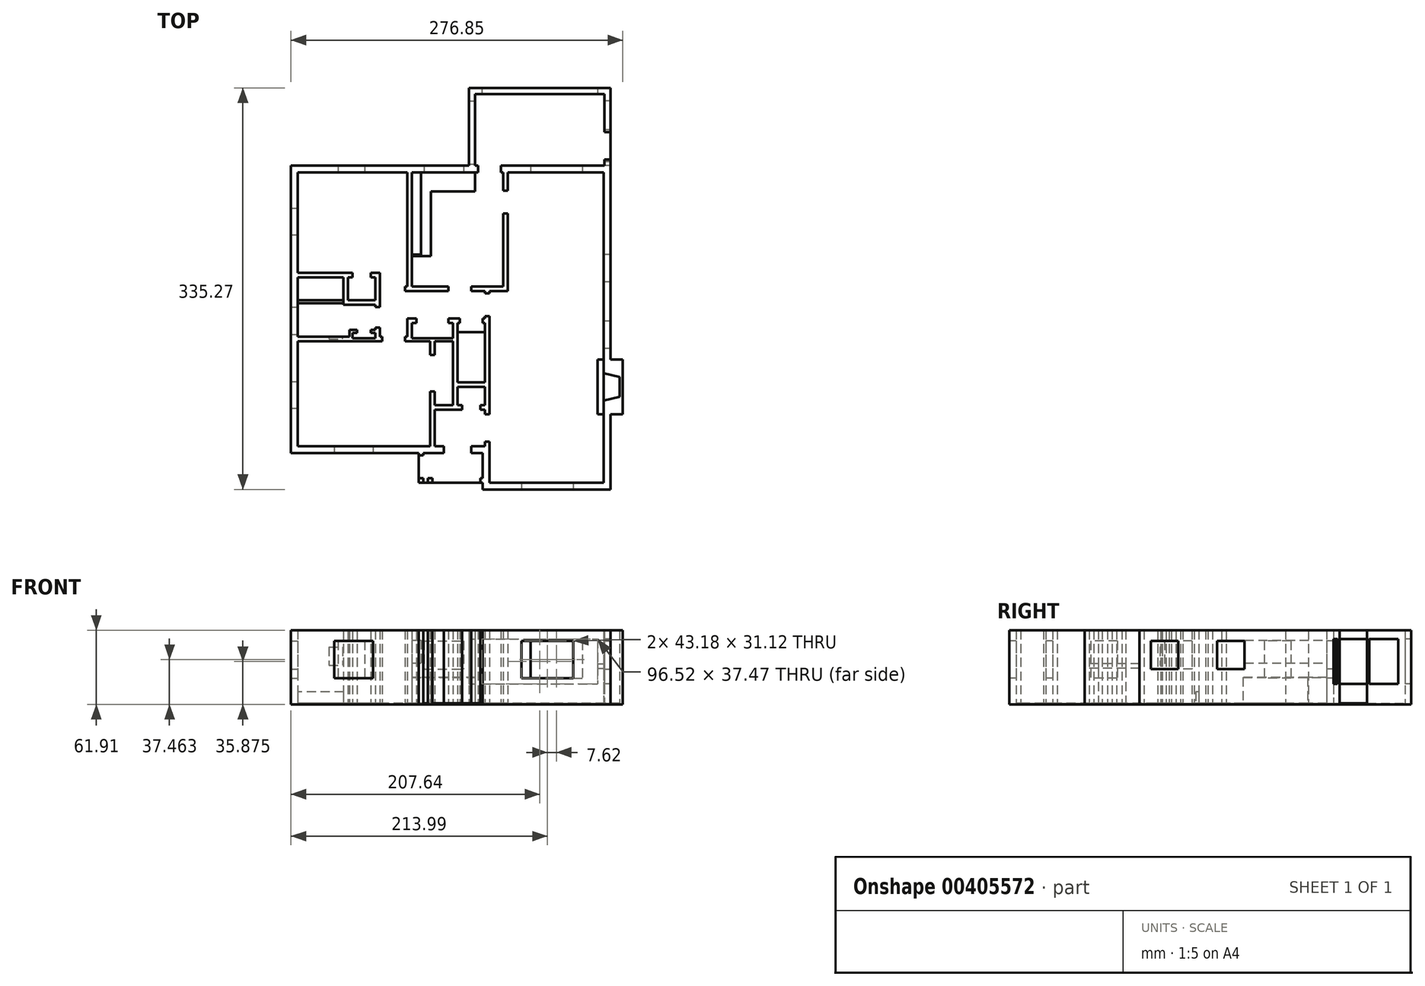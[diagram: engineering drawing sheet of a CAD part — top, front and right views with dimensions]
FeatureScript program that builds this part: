
annotation { "Feature Type Name" : "Feature", "Feature Type Description" : "" }
export const myFeature = defineFeature(function(context is Context, id is Id, definition is map)
    precondition{}
    {
        {
            var Q0;
            Q0=qCreatedBy(makeId("Top.planeOp"),FACE);
            var sketch = newSketch(context, id + "F0", { "sketchPlane" : qUnion([Q0])});
            skLineSegment(sketch, "E0.bottom", {"start": v(0, 0) * mm, "end": v(3810, 0) * mm});
            skLineSegment(sketch, "E0.top", {"start": v(-6400.8, 10363.2) * mm, "end": v(-2743.2, 10363.2) * mm});
            skLineSegment(sketch, "E0.left", {"start": v(0, 0) * mm, "end": v(0, 1219.2) * mm});
            skLineSegment(sketch, "E0.right", {"start": v(3810, 0) * mm, "end": v(3810, 10363.2) * mm});
            skLineSegment(sketch, "E1.bottom", {"start": v(-152.4, 1219.2) * mm, "end": v(-609.6, 1219.2) * mm});
            skLineSegment(sketch, "E1.right", {"start": v(-6400.8, 1219.2) * mm, "end": v(-6400.8, 4724.4) * mm});
            skLineSegment(sketch, "E2.0", {"start": v(-6629.4, 990.6) * mm, "end": v(-6629.4, 10591.8) * mm});
            skLineSegment(sketch, "E2.1", {"start": v(4038.6, -228.6) * mm, "end": v(4038.6, 10591.8) * mm});
            skLineSegment(sketch, "E2.2", {"start": v(-228.6, -228.6) * mm, "end": v(4038.6, -228.6) * mm});
            skLineSegment(sketch, "E2.3", {"start": v(-6629.4, 10591.8) * mm, "end": v(-381, 10591.8) * mm});
            skLineSegment(sketch, "E2.4", {"start": v(-228.6, -228.6) * mm, "end": v(-228.6, 990.6) * mm});
            skLineSegment(sketch, "E2.5", {"start": v(-228.6, 990.6) * mm, "end": v(-609.6, 990.6) * mm});
            skLineSegment(sketch, "E3", {"start": v(-1981.2, 1219.2) * mm, "end": v(-1981.2, 3048) * mm});
            skLineSegment(sketch, "E4", {"start": v(-1981.2, 3048) * mm, "end": v(-1828.8, 3048) * mm});
            skLineSegment(sketch, "E5", {"start": v(-1828.8, 3048) * mm, "end": v(-1828.8, 2590.8) * mm});
            skLineSegment(sketch, "E6", {"start": v(-1828.8, 2590.8) * mm, "end": v(-1219.2, 2590.8) * mm});
            skLineSegment(sketch, "E7", {"start": v(-1219.2, 2590.8) * mm, "end": v(-1219.2, 4724.4) * mm});
            skLineSegment(sketch, "E8", {"start": v(-1219.2, 4724.4) * mm, "end": v(-1828.8, 4724.4) * mm});
            skLineSegment(sketch, "E9", {"start": v(-1828.8, 4724.4) * mm, "end": v(-1828.8, 4267.2) * mm});
            skLineSegment(sketch, "E10", {"start": v(-1828.8, 4267.2) * mm, "end": v(-1981.2, 4267.2) * mm});
            skLineSegment(sketch, "E11", {"start": v(-1981.2, 4267.2) * mm, "end": v(-1981.2, 4724.4) * mm});
            skLineSegment(sketch, "E12", {"start": v(-1981.2, 4724.4) * mm, "end": v(-2819.4, 4724.4) * mm});
            skLineSegment(sketch, "E13", {"start": v(-2819.4, 4724.4) * mm, "end": v(-2819.4, 4876.8) * mm});
            skLineSegment(sketch, "E14", {"start": v(-2819.4, 4876.8) * mm, "end": v(-2743.2, 4876.8) * mm});
            skLineSegment(sketch, "E15", {"start": v(-2743.2, 4876.8) * mm, "end": v(-2743.2, 5486.4) * mm});
            skLineSegment(sketch, "E16", {"start": v(-2743.2, 5486.4) * mm, "end": v(-2438.4, 5486.4) * mm});
            skLineSegment(sketch, "E17", {"start": v(-2438.4, 5486.4) * mm, "end": v(-2438.4, 5334) * mm});
            skLineSegment(sketch, "E18", {"start": v(-2438.4, 5334) * mm, "end": v(-2590.8, 5334) * mm});
            skLineSegment(sketch, "E19", {"start": v(-2590.8, 5334) * mm, "end": v(-2590.8, 4826) * mm});
            skLineSegment(sketch, "E20", {"start": v(-2590.8, 4826) * mm, "end": v(-1219.2, 4826) * mm});
            skLineSegment(sketch, "E21", {"start": v(-1219.2, 4826) * mm, "end": v(-1219.2, 5334) * mm});
            skLineSegment(sketch, "E22", {"start": v(-1219.2, 5334) * mm, "end": v(-1371.6, 5334) * mm});
            skLineSegment(sketch, "E23", {"start": v(-1371.6, 5334) * mm, "end": v(-1371.6, 5486.4) * mm});
            skLineSegment(sketch, "E24", {"start": v(-1371.6, 5486.4) * mm, "end": v(-990.6, 5486.4) * mm});
            skLineSegment(sketch, "E25", {"start": v(-990.6, 5486.4) * mm, "end": v(-990.6, 5334) * mm});
            skLineSegment(sketch, "E26", {"start": v(-990.6, 5334) * mm, "end": v(-1066.8, 5334) * mm});
            skLineSegment(sketch, "E27", {"start": v(-1066.8, 5334) * mm, "end": v(-1066.8, 3352.8) * mm});
            skLineSegment(sketch, "E28", {"start": v(-1066.8, 2590.8) * mm, "end": v(-914.4, 2590.8) * mm});
            skLineSegment(sketch, "E29", {"start": v(-914.4, 2590.8) * mm, "end": v(-914.4, 2438.4) * mm});
            skLineSegment(sketch, "E30", {"start": v(-914.4, 2438.4) * mm, "end": v(-1828.8, 2438.4) * mm});
            skLineSegment(sketch, "E31", {"start": v(-1828.8, 2438.4) * mm, "end": v(-1828.8, 1219.2) * mm});
            skLineSegment(sketch, "E32", {"start": v(-1524, 1219.2) * mm, "end": v(-1524, 990.6) * mm});
            skLineSegment(sketch, "E33", {"start": v(-609.6, 990.6) * mm, "end": v(-609.6, 1219.2) * mm});
            skLineSegment(sketch, "E34.trimOffspring", {"start": v(-1524, 1219.2) * mm, "end": v(-1828.8, 1219.2) * mm});
            skLineSegment(sketch, "E35.trimOffspring", {"start": v(-1524, 990.6) * mm, "end": v(-6629.4, 990.6) * mm});
            skLineSegment(sketch, "E36", {"start": v(-3581.4, 4724.4) * mm, "end": v(-6400.8, 4724.4) * mm});
            skLineSegment(sketch, "E37", {"start": v(-6400.8, 4876.8) * mm, "end": v(-5359.4, 4876.8) * mm});
            skLineSegment(sketch, "E38", {"start": v(-5359.4, 4876.8) * mm, "end": v(-5359.4, 4800.6) * mm});
            skLineSegment(sketch, "E39", {"start": v(-5359.4, 4800.6) * mm, "end": v(-4902.2, 4800.6) * mm});
            skLineSegment(sketch, "E40", {"start": v(-4902.2, 4800.6) * mm, "end": v(-4902.2, 4876.8) * mm});
            skLineSegment(sketch, "E41", {"start": v(-4902.2, 4876.8) * mm, "end": v(-4673.6, 4876.8) * mm});
            skLineSegment(sketch, "E42", {"start": v(-4673.6, 4876.8) * mm, "end": v(-4673.6, 5105.4) * mm});
            skLineSegment(sketch, "E43", {"start": v(-4673.6, 5105.4) * mm, "end": v(-4419.6, 5105.4) * mm});
            skLineSegment(sketch, "E44", {"start": v(-4419.6, 5105.4) * mm, "end": v(-4419.6, 5003.8) * mm});
            skLineSegment(sketch, "E45", {"start": v(-4419.6, 5003.8) * mm, "end": v(-4572, 5003.8) * mm});
            skLineSegment(sketch, "E46", {"start": v(-4572, 5003.8) * mm, "end": v(-4572, 4826) * mm});
            skLineSegment(sketch, "E47", {"start": v(-4572, 4826) * mm, "end": v(-3810, 4826) * mm});
            skLineSegment(sketch, "E48", {"start": v(-3810, 4826) * mm, "end": v(-3810, 5003.8) * mm});
            skLineSegment(sketch, "E49", {"start": v(-3810, 5003.8) * mm, "end": v(-3962.4, 5003.8) * mm});
            skLineSegment(sketch, "E50", {"start": v(-3962.4, 5003.8) * mm, "end": v(-3962.4, 5105.4) * mm});
            skLineSegment(sketch, "E51", {"start": v(-3962.4, 5105.4) * mm, "end": v(-3810, 5105.4) * mm});
            skLineSegment(sketch, "E52", {"start": v(-3810, 5105.4) * mm, "end": v(-3810, 5181.6) * mm});
            skLineSegment(sketch, "E53", {"start": v(-3810, 5181.6) * mm, "end": v(-3657.6, 5181.6) * mm});
            skLineSegment(sketch, "E54", {"start": v(-3657.6, 5181.6) * mm, "end": v(-3657.6, 4876.8) * mm});
            skLineSegment(sketch, "E55", {"start": v(-3657.6, 4876.8) * mm, "end": v(-3581.4, 4876.8) * mm});
            skLineSegment(sketch, "E56", {"start": v(-3581.4, 4876.8) * mm, "end": v(-3581.4, 4724.4) * mm});
            skLineSegment(sketch, "E57", {"start": v(-152.4, 1219.2) * mm, "end": v(-152.4, 1371.6) * mm});
            skLineSegment(sketch, "E58", {"start": v(-152.4, 1371.6) * mm, "end": v(0, 1371.6) * mm});
            skLineSegment(sketch, "E59", {"start": v(0, 1371.6) * mm, "end": v(0, 1219.2) * mm});
            skLineSegment(sketch, "E60", {"start": v(0, 2286) * mm, "end": v(-152.4, 2286) * mm});
            skLineSegment(sketch, "E61", {"start": v(-152.4, 2286) * mm, "end": v(-152.4, 2438.4) * mm});
            skLineSegment(sketch, "E62", {"start": v(-152.4, 2438.4) * mm, "end": v(-304.8, 2438.4) * mm});
            skLineSegment(sketch, "E63", {"start": v(-304.8, 2438.4) * mm, "end": v(-304.8, 2590.8) * mm});
            skLineSegment(sketch, "E64", {"start": v(-304.8, 2590.8) * mm, "end": v(-152.4, 2590.8) * mm});
            skLineSegment(sketch, "E65", {"start": v(-152.4, 2590.8) * mm, "end": v(-152.4, 3200.4) * mm});
            skLineSegment(sketch, "E66", {"start": v(-152.4, 3200.4) * mm, "end": v(-1066.8, 3200.4) * mm});
            skLineSegment(sketch, "E67", {"start": v(-1066.8, 3352.8) * mm, "end": v(-152.4, 3352.8) * mm});
            skLineSegment(sketch, "E68", {"start": v(-152.4, 3352.8) * mm, "end": v(-152.4, 5334) * mm});
            skLineSegment(sketch, "E69", {"start": v(-152.4, 5334) * mm, "end": v(-228.6, 5334) * mm});
            skLineSegment(sketch, "E70", {"start": v(-228.6, 5334) * mm, "end": v(-228.6, 5486.4) * mm});
            skLineSegment(sketch, "E71", {"start": v(-228.6, 5486.4) * mm, "end": v(-152.4, 5486.4) * mm});
            skLineSegment(sketch, "E72", {"start": v(-152.4, 5486.4) * mm, "end": v(-152.4, 5562.6) * mm});
            skLineSegment(sketch, "E73", {"start": v(-152.4, 5562.6) * mm, "end": v(0, 5562.6) * mm});
            skLineSegment(sketch, "E74", {"start": v(0, 5562.6) * mm, "end": v(0, 2286) * mm});
            skLineSegment(sketch, "E75.trimOffspring", {"start": v(-1066.8, 3200.4) * mm, "end": v(-1066.8, 2590.8) * mm});
            skLineSegment(sketch, "E76", {"start": v(457.2, 10363.2) * mm, "end": v(457.2, 9753.6) * mm});
            skLineSegment(sketch, "E77", {"start": v(457.2, 9753.6) * mm, "end": v(609.6, 9753.6) * mm});
            skLineSegment(sketch, "E78", {"start": v(609.6, 9753.6) * mm, "end": v(609.6, 10363.2) * mm});
            skLineSegment(sketch, "E79", {"start": v(457.2, 8991.6) * mm, "end": v(457.2, 6553.2) * mm});
            skLineSegment(sketch, "E80", {"start": v(457.2, 6553.2) * mm, "end": v(-609.6, 6553.2) * mm});
            skLineSegment(sketch, "E81", {"start": v(-609.6, 6553.2) * mm, "end": v(-609.6, 6400.8) * mm});
            skLineSegment(sketch, "E82", {"start": v(-609.6, 6400.8) * mm, "end": v(-152.4, 6400.8) * mm});
            skLineSegment(sketch, "E83", {"start": v(-152.4, 6400.8) * mm, "end": v(-152.4, 6324.6) * mm});
            skLineSegment(sketch, "E84", {"start": v(-152.4, 6324.6) * mm, "end": v(0, 6324.6) * mm});
            skLineSegment(sketch, "E85", {"start": v(0, 6324.6) * mm, "end": v(0, 6400.8) * mm});
            skLineSegment(sketch, "E86", {"start": v(0, 6400.8) * mm, "end": v(609.6, 6400.8) * mm});
            skLineSegment(sketch, "E87", {"start": v(609.6, 6400.8) * mm, "end": v(609.6, 8991.6) * mm});
            skLineSegment(sketch, "E88", {"start": v(609.6, 8991.6) * mm, "end": v(457.2, 8991.6) * mm});
            skLineSegment(sketch, "E89", {"start": v(-1371.6, 6553.2) * mm, "end": v(-1371.6, 6400.8) * mm});
            skLineSegment(sketch, "E90", {"start": v(-1371.6, 6400.8) * mm, "end": v(-2819.4, 6400.8) * mm});
            skLineSegment(sketch, "E91", {"start": v(-2819.4, 6400.8) * mm, "end": v(-2819.4, 6553.2) * mm});
            skLineSegment(sketch, "E92", {"start": v(-2819.4, 6553.2) * mm, "end": v(-2743.2, 6553.2) * mm});
            skLineSegment(sketch, "E93", {"start": v(-2743.2, 6553.2) * mm, "end": v(-2743.2, 10363.2) * mm});
            skLineSegment(sketch, "E94", {"start": v(-2590.8, 10363.2) * mm, "end": v(-2590.8, 6553.2) * mm});
            skLineSegment(sketch, "E95", {"start": v(-2590.8, 6553.2) * mm, "end": v(-1371.6, 6553.2) * mm});
            skLineSegment(sketch, "E96", {"start": v(-6400.8, 7010.4) * mm, "end": v(-4572, 7010.4) * mm});
            skLineSegment(sketch, "E97", {"start": v(-4572, 7010.4) * mm, "end": v(-4572, 6858) * mm});
            skLineSegment(sketch, "E98", {"start": v(-4572, 6858) * mm, "end": v(-4724.4, 6858) * mm});
            skLineSegment(sketch, "E99", {"start": v(-4724.4, 6858) * mm, "end": v(-4724.4, 6096) * mm});
            skLineSegment(sketch, "E100", {"start": v(-4724.4, 6096) * mm, "end": v(-3810, 6096) * mm});
            skLineSegment(sketch, "E101", {"start": v(-3810, 6096) * mm, "end": v(-3810, 6858) * mm});
            skLineSegment(sketch, "E102", {"start": v(-3810, 6858) * mm, "end": v(-3962.4, 6858) * mm});
            skLineSegment(sketch, "E103", {"start": v(-3962.4, 6858) * mm, "end": v(-3962.4, 7010.4) * mm});
            skLineSegment(sketch, "E104", {"start": v(-3962.4, 7010.4) * mm, "end": v(-3657.6, 7010.4) * mm});
            skLineSegment(sketch, "E105", {"start": v(-3657.6, 7010.4) * mm, "end": v(-3657.6, 5867.4) * mm});
            skLineSegment(sketch, "E106", {"start": v(-3657.6, 5867.4) * mm, "end": v(-3810, 5867.4) * mm});
            skLineSegment(sketch, "E107", {"start": v(-3810, 5867.4) * mm, "end": v(-3810, 5943.6) * mm});
            skLineSegment(sketch, "E108", {"start": v(-3810, 5943.6) * mm, "end": v(-4876.8, 5943.6) * mm});
            skLineSegment(sketch, "E109", {"start": v(-4876.8, 5943.6) * mm, "end": v(-4876.8, 6858) * mm});
            skLineSegment(sketch, "E110", {"start": v(-4876.8, 6858) * mm, "end": v(-6400.8, 6858) * mm});
            skText(sketch, "E111", { "text": "All doors are 80in tall", "fontName": "OpenSans-Regular.ttf"});
            skLineSegment(sketch, "E112", {"start": v(381, 10363.2) * mm, "end": v(381, 10591.8) * mm});
            skLineSegment(sketch, "E113", {"start": v(-381, 10363.2) * mm, "end": v(-381, 10591.8) * mm});
            skLineSegment(sketch, "E114.trimOffspring", {"start": v(381, 10591.8) * mm, "end": v(4038.6, 10591.8) * mm});
            skLineSegment(sketch, "E115.trimOffspring", {"start": v(381, 10363.2) * mm, "end": v(457.2, 10363.2) * mm});
            skLineSegment(sketch, "E116", {"start": v(-5359.4, 4876.8) * mm, "end": v(-4902.2, 4876.8) * mm});
            skLineSegment(sketch, "E117", {"start": v(-4876.8, 5994.4) * mm, "end": v(-6400.8, 5994.4) * mm});
            skLineSegment(sketch, "E118", {"start": v(-6400.8, 6070.6) * mm, "end": v(-4876.8, 6070.6) * mm});
            skLineSegment(sketch, "E119", {"start": v(4038.6, 2286) * mm, "end": v(4445, 2286) * mm});
            skLineSegment(sketch, "E120", {"start": v(4445, 2286) * mm, "end": v(4445, 4114.8) * mm});
            skLineSegment(sketch, "E121", {"start": v(4445, 4114.8) * mm, "end": v(4038.6, 4114.8) * mm});
            skLineSegment(sketch, "E122", {"start": v(3810, 3657.6) * mm, "end": v(4343.4, 3530.6) * mm});
            skLineSegment(sketch, "E123", {"start": v(4343.4, 3530.6) * mm, "end": v(4343.4, 2870.2) * mm});
            skLineSegment(sketch, "E124", {"start": v(4343.4, 2870.2) * mm, "end": v(3810, 2743.2) * mm});
            skLineSegment(sketch, "E125", {"start": v(4343.4, 3200.4) * mm, "end": v(4445, 3200.4) * mm, "construction": true});
            skLineSegment(sketch, "E126.trimOffspring", {"start": v(-1981.2, 1219.2) * mm, "end": v(-6400.8, 1219.2) * mm});
            skLineSegment(sketch, "E127.trimOffspring", {"start": v(-2590.8, 10363.2) * mm, "end": v(-381, 10363.2) * mm});
            skLineSegment(sketch, "E128.trimOffspring", {"start": v(609.6, 10363.2) * mm, "end": v(3810, 10363.2) * mm});
            skLineSegment(sketch, "E129.trimOffspring", {"start": v(-6400.8, 4876.8) * mm, "end": v(-6400.8, 6858) * mm});
            skLineSegment(sketch, "E130.trimOffspring", {"start": v(-6400.8, 7010.4) * mm, "end": v(-6400.8, 10363.2) * mm});
            skLineSegment(sketch, "E131", {"start": v(4038.6, 10591.8) * mm, "end": v(4038.6, 13182.6) * mm});
            skLineSegment(sketch, "E132", {"start": v(4038.6, 13182.6) * mm, "end": v(-685.8, 13182.6) * mm});
            skLineSegment(sketch, "E133", {"start": v(-685.8, 13182.6) * mm, "end": v(-685.8, 10591.8) * mm});
            skLineSegment(sketch, "E134", {"start": v(3835.4, 10591.8) * mm, "end": v(3835.4, 12979.4) * mm});
            skLineSegment(sketch, "E135", {"start": v(3835.4, 12979.4) * mm, "end": v(-482.6, 12979.4) * mm});
            skLineSegment(sketch, "E136", {"start": v(-482.6, 12979.4) * mm, "end": v(-482.6, 10591.8) * mm});
            skLineSegment(sketch, "E137", {"start": v(-2362.2, 990.6) * mm, "end": v(-2362.2, 0) * mm});
            skLineSegment(sketch, "E138", {"start": v(-2362.2, 0) * mm, "end": v(-228.6, 0) * mm});
            skLineSegment(sketch, "E139", {"start": v(-2362.2, 152.4) * mm, "end": v(-2209.8, 152.4) * mm});
            skLineSegment(sketch, "E140", {"start": v(-2209.8, 152.4) * mm, "end": v(-2209.8, 0) * mm});
            skLineSegment(sketch, "E141", {"start": v(-2057.4, 0) * mm, "end": v(-2057.4, 152.4) * mm});
            skLineSegment(sketch, "E142", {"start": v(-2057.4, 152.4) * mm, "end": v(-1905, 152.4) * mm});
            skLineSegment(sketch, "E143", {"start": v(-1905, 152.4) * mm, "end": v(-1905, 0) * mm});
            skLineSegment(sketch, "E144", {"start": v(-304.8, 0) * mm, "end": v(-304.8, 152.4) * mm});
            skLineSegment(sketch, "E145", {"start": v(-304.8, 152.4) * mm, "end": v(-228.6, 152.4) * mm});
            skLineSegment(sketch, "E146", {"start": v(-2209.8, 990.6) * mm, "end": v(-2209.8, 914.4) * mm});
            skLineSegment(sketch, "E147", {"start": v(-2209.8, 914.4) * mm, "end": v(-2362.2, 914.4) * mm});
            skLineSegment(sketch, "E148", {"start": v(3835.4, 10795) * mm, "end": v(4038.6, 10795) * mm});
            skLineSegment(sketch, "E149", {"start": v(3835.4, 11709.4) * mm, "end": v(4038.6, 11709.4) * mm});
            const initialGuessF0  = {"E111": [1.17516, -1.09779, 1, 0, 0.12028]};
            skSetInitialGuess(sketch, initialGuessF0);
            skSolve(sketch);
        }
        {
            var Q0;
            {var subQ3=sQuery(id+"F0.wireOp",EDGE,"E132");Q0=makeQuery(id+"F0.imprint","IMPRINT",FACE,{"disambiguationData":[TD([[makeQuery(id+"F0.imprint","IMPRINT",EDGE,{"derivedFrom":subQ3}),1.0]])]});}
            var Q1;
            {var subQ5=sQuery(id+"F0.wireOp",EDGE,"E148");Q1=makeQuery(id+"F0.imprint","IMPRINT",FACE,{"disambiguationData":[TD([[makeQuery(id+"F0.imprint","IMPRINT",EDGE,{"derivedFrom":subQ5}),-1.0]])]});}
            var Q2;
            Q2=makeQuery(id+"F0.imprint","IMPRINT",FACE,{"disambiguationData":[TD([[makeQuery(id+"F0.imprint","IMPRINT",EDGE,{"derivedFrom":sQuery(id+"F0.wireOp",EDGE,"E76")}),1.0]])]});
            var Q3;
            Q3=makeQuery(id+"F0.imprint","IMPRINT",FACE,{"disambiguationData":[TD([[makeQuery(id+"F0.imprint","IMPRINT",EDGE,{"derivedFrom":sQuery(id+"F0.wireOp",EDGE,"E0.top")}),1.0]])]});
            var Q4;
            Q4=makeQuery(id+"F0.imprint","IMPRINT",FACE,{"disambiguationData":[TD([[makeQuery(id+"F0.imprint","IMPRINT",EDGE,{"derivedFrom":sQuery(id+"F0.wireOp",EDGE,"E79")}),1.0]])]});
            var Q5;
            {var subQ0=sQuery(id+"F0.wireOp",EDGE,"E119");Q5=makeQuery(id+"F0.imprint","IMPRINT",FACE,{"disambiguationData":[TD([[makeQuery(id+"F0.imprint","IMPRINT",EDGE,{"derivedFrom":subQ0}),1.0]])]});}
            var Q6;
            {var subQ11=sQuery(id+"F0.wireOp",EDGE,"E0.bottom");Q6=makeQuery(id+"F0.imprint","IMPRINT",FACE,{"disambiguationData":[TD([[makeQuery(id+"F0.imprint","IMPRINT",EDGE,{"derivedFrom":subQ11}),-1.0]])]});}
            var Q7;
            Q7=makeQuery(id+"F0.imprint","IMPRINT",FACE,{"disambiguationData":[TD([[makeQuery(id+"F0.imprint","IMPRINT",EDGE,{"derivedFrom":sQuery(id+"F0.wireOp",EDGE,"E38")}),1.0]])]});
            var Q8;
            {var subQ3=sQuery(id+"F0.wireOp",EDGE,"E139");Q8=makeQuery(id+"F0.imprint","IMPRINT",FACE,{"disambiguationData":[TD([[makeQuery(id+"F0.imprint","IMPRINT",EDGE,{"derivedFrom":subQ3}),-1.0]])]});}
            var Q9;
            {var subQ0=sQuery(id+"F0.wireOp",EDGE,"E141");Q9=makeQuery(id+"F0.imprint","IMPRINT",FACE,{"disambiguationData":[TD([[makeQuery(id+"F0.imprint","IMPRINT",EDGE,{"derivedFrom":subQ0}),-1.0]])]});}
            var Q10;
            {var subQ3=sQuery(id+"F0.wireOp",EDGE,"E146");Q10=makeQuery(id+"F0.imprint","IMPRINT",FACE,{"disambiguationData":[TD([[makeQuery(id+"F0.imprint","IMPRINT",EDGE,{"derivedFrom":subQ3}),-1.0]])]});}
            var Q11;
            {var subQ4=sQuery(id+"F0.wireOp",EDGE,"E144");Q11=makeQuery(id+"F0.imprint","IMPRINT",FACE,{"disambiguationData":[TD([[makeQuery(id+"F0.imprint","IMPRINT",EDGE,{"derivedFrom":subQ4}),-1.0]])]});}
            extrude(context, id + "F1", {"entities" : qUnion([Q0, Q1, Q2, Q3, Q4, Q5, Q6, Q7, Q8, Q9, Q10, Q11]), "depth" : 2438.4 * mm, "offsetDistance" : 25.4 * mm});
        }
        {
            var Q0;
            {var subQ5=sQuery(id+"F0.wireOp",EDGE,"E123");Q0=makeQuery(id+"F0.imprint","IMPRINT",FACE,{"disambiguationData":[TD([[makeQuery(id+"F0.imprint","IMPRINT",EDGE,{"derivedFrom":subQ5}),-1.0]])]});}
            var Q1;
            {var subQ0=sQuery(id+"F0.wireOp",EDGE,"E122");var subQ1=sQuery(id+"F0.wireOp",EDGE,"E0.right");var subQ2=makeQuery(id+"F0.imprint","INTERSECT",VERTEX,{"derivedFrom":[subQ1,subQ0]});Q1=makeQuery(id+"F0.imprint","IMPRINT",FACE,{"disambiguationData":[TD([[makeQuery(id+"F0.imprint","IMPRINT",EDGE,{"disambiguationData":[TD([[subQ2,1.0]])],"derivedFrom":subQ1}),-1.0]])]});}
            var Q2;
            Q2=makeQuery(id+"F0.imprint","IMPRINT",FACE,{"disambiguationData":[TD([[makeQuery(id+"F0.imprint","IMPRINT",EDGE,{"derivedFrom":sQuery(id+"F0.wireOp",EDGE,"E79")}),1.0]])]});
            var Q3;
            {var subQ0=sQuery(id+"F0.wireOp",EDGE,"E110");Q3=makeQuery(id+"F0.imprint","IMPRINT",FACE,{"disambiguationData":[TD([[makeQuery(id+"F0.imprint","IMPRINT",EDGE,{"derivedFrom":subQ0}),1.0]])]});}
            var Q4;
            {var subQ0=sQuery(id+"F0.wireOp",EDGE,"E117");Q4=makeQuery(id+"F0.imprint","IMPRINT",FACE,{"disambiguationData":[TD([[makeQuery(id+"F0.imprint","IMPRINT",EDGE,{"derivedFrom":subQ0}),-1.0]])]});}
            var Q5;
            Q5=makeQuery(id+"F0.imprint","IMPRINT",FACE,{"disambiguationData":[TD([[makeQuery(id+"F0.imprint","IMPRINT",EDGE,{"derivedFrom":sQuery(id+"F0.wireOp",EDGE,"E38")}),1.0]])]});
            var Q6;
            {var subQ19=sQuery(id+"F0.wireOp",EDGE,"E0.bottom");Q6=makeQuery(id+"F0.imprint","IMPRINT",FACE,{"disambiguationData":[TD([[makeQuery(id+"F0.imprint","IMPRINT",EDGE,{"derivedFrom":subQ19}),1.0]])]});}
            var Q7;
            Q7=makeQuery(id+"F0.imprint","IMPRINT",FACE,{"disambiguationData":[TD([[makeQuery(id+"F0.imprint","IMPRINT",EDGE,{"derivedFrom":sQuery(id+"F0.wireOp",EDGE,"E0.top")}),1.0]])]});
            var Q8;
            {var subQ3=sQuery(id+"F0.wireOp",EDGE,"E146");Q8=makeQuery(id+"F0.imprint","IMPRINT",FACE,{"disambiguationData":[TD([[makeQuery(id+"F0.imprint","IMPRINT",EDGE,{"derivedFrom":subQ3}),-1.0]])]});}
            var Q9;
            {var subQ3=sQuery(id+"F0.wireOp",EDGE,"E139");Q9=makeQuery(id+"F0.imprint","IMPRINT",FACE,{"disambiguationData":[TD([[makeQuery(id+"F0.imprint","IMPRINT",EDGE,{"derivedFrom":subQ3}),-1.0]])]});}
            var Q10;
            {var subQ0=sQuery(id+"F0.wireOp",EDGE,"E141");Q10=makeQuery(id+"F0.imprint","IMPRINT",FACE,{"disambiguationData":[TD([[makeQuery(id+"F0.imprint","IMPRINT",EDGE,{"derivedFrom":subQ0}),-1.0]])]});}
            var Q11;
            {var subQ3=sQuery(id+"F0.wireOp",EDGE,"E132");Q11=makeQuery(id+"F0.imprint","IMPRINT",FACE,{"disambiguationData":[TD([[makeQuery(id+"F0.imprint","IMPRINT",EDGE,{"derivedFrom":subQ3}),1.0]])]});}
            var Q12;
            {var subQ0=sQuery(id+"F0.wireOp",EDGE,"E148");Q12=makeQuery(id+"F0.imprint","IMPRINT",FACE,{"disambiguationData":[TD([[makeQuery(id+"F0.imprint","IMPRINT",EDGE,{"derivedFrom":subQ0}),1.0]])]});}
            var Q13;
            Q13=makeQuery(id+"F0.imprint","IMPRINT",FACE,{"disambiguationData":[TD([[makeQuery(id+"F0.imprint","IMPRINT",EDGE,{"derivedFrom":sQuery(id+"F0.wireOp",EDGE,"E76")}),1.0]])]});
            var Q14;
            {var subQ5=sQuery(id+"F0.wireOp",EDGE,"E148");Q14=makeQuery(id+"F0.imprint","IMPRINT",FACE,{"disambiguationData":[TD([[makeQuery(id+"F0.imprint","IMPRINT",EDGE,{"derivedFrom":subQ5}),-1.0]])]});}
            var Q15;
            {var subQ0=sQuery(id+"F0.wireOp",EDGE,"E119");Q15=makeQuery(id+"F0.imprint","IMPRINT",FACE,{"disambiguationData":[TD([[makeQuery(id+"F0.imprint","IMPRINT",EDGE,{"derivedFrom":subQ0}),1.0]])]});}
            var Q16;
            {var subQ11=sQuery(id+"F0.wireOp",EDGE,"E0.bottom");Q16=makeQuery(id+"F0.imprint","IMPRINT",FACE,{"disambiguationData":[TD([[makeQuery(id+"F0.imprint","IMPRINT",EDGE,{"derivedFrom":subQ11}),-1.0]])]});}
            var Q17;
            {var subQ4=sQuery(id+"F0.wireOp",EDGE,"E144");Q17=makeQuery(id+"F0.imprint","IMPRINT",FACE,{"disambiguationData":[TD([[makeQuery(id+"F0.imprint","IMPRINT",EDGE,{"derivedFrom":subQ4}),-1.0]])]});}
            extrude(context, id + "F2", {"entities" : qUnion([Q0, Q1, Q2, Q3, Q4, Q5, Q6, Q7, Q8, Q9, Q10, Q11, Q12, Q13, Q14, Q15, Q16, Q17]), "operationType" : NewBodyOperationType.ADD, "oppositeDirection" : true, "depth" : 38.1 * mm, "offsetDistance" : 25.4 * mm});
        }
        {
            var Q0;
            Q0=qCreatedBy(makeId("Top.planeOp"),FACE);
            var sketch = newSketch(context, id + "F3", { "sketchPlane" : qUnion([Q0])});
            skLineSegment(sketch, "E150", {"start": v(-482.6, 10363.2) * mm, "end": v(-482.6, 9728.2) * mm});
            skLineSegment(sketch, "E151", {"start": v(-482.6, 9728.2) * mm, "end": v(-1955.8, 9728.2) * mm});
            skLineSegment(sketch, "E152", {"start": v(-1955.8, 9728.2) * mm, "end": v(-1955.8, 7569.2) * mm});
            skLineSegment(sketch, "E153", {"start": v(-1955.8, 7569.2) * mm, "end": v(-2590.8, 7569.2) * mm});
            skLineSegment(sketch, "E154", {"start": v(-2590.8, 7569.2) * mm, "end": v(-2590.8, 10363.2) * mm});
            skLineSegment(sketch, "E155", {"start": v(-2590.8, 10363.2) * mm, "end": v(-482.6, 10363.2) * mm});
            skLineSegment(sketch, "E156", {"start": v(-1955.8, 7569.2) * mm, "end": v(-1879.6, 7569.2) * mm});
            skLineSegment(sketch, "E157", {"start": v(-1879.6, 7569.2) * mm, "end": v(-1879.6, 6807.2) * mm});
            skLineSegment(sketch, "E158", {"start": v(-1879.6, 6807.2) * mm, "end": v(-2590.8, 6807.2) * mm});
            skLineSegment(sketch, "E159", {"start": v(-2590.8, 6807.2) * mm, "end": v(-2590.8, 7569.2) * mm});
            skLineSegment(sketch, "E160.bottom", {"start": v(457.2, 6908.8) * mm, "end": v(-457.2, 6908.8) * mm});
            skLineSegment(sketch, "E160.top", {"start": v(457.2, 7823.2) * mm, "end": v(-457.2, 7823.2) * mm});
            skLineSegment(sketch, "E160.left", {"start": v(457.2, 6908.8) * mm, "end": v(457.2, 7823.2) * mm});
            skLineSegment(sketch, "E160.right", {"start": v(-457.2, 6908.8) * mm, "end": v(-457.2, 7823.2) * mm});
            skLineSegment(sketch, "E161.bottom", {"start": v(0, 7823.2) * mm, "end": v(457.2, 7823.2) * mm});
            skLineSegment(sketch, "E161.top", {"start": v(0, 8737.6) * mm, "end": v(457.2, 8737.6) * mm});
            skLineSegment(sketch, "E161.left", {"start": v(0, 7823.2) * mm, "end": v(0, 8737.6) * mm});
            skLineSegment(sketch, "E161.right", {"start": v(457.2, 7823.2) * mm, "end": v(457.2, 8737.6) * mm});
            skLineSegment(sketch, "E162.bottom", {"start": v(-2590.8, 10363.2) * mm, "end": v(-2286, 10363.2) * mm});
            skLineSegment(sketch, "E162.top", {"start": v(-2590.8, 7620) * mm, "end": v(-2286, 7620) * mm});
            skLineSegment(sketch, "E162.left", {"start": v(-2590.8, 10363.2) * mm, "end": v(-2590.8, 7620) * mm});
            skLineSegment(sketch, "E162.right", {"start": v(-2286, 10363.2) * mm, "end": v(-2286, 7620) * mm});
            skLineSegment(sketch, "E163.bottom", {"start": v(-5054.6, 10591.8) * mm, "end": v(-4165.6, 10591.8) * mm});
            skLineSegment(sketch, "E163.top", {"start": v(-5054.6, 10363.2) * mm, "end": v(-4165.6, 10363.2) * mm});
            skLineSegment(sketch, "E163.left", {"start": v(-5054.6, 10591.8) * mm, "end": v(-5054.6, 10363.2) * mm});
            skLineSegment(sketch, "E163.right", {"start": v(-4165.6, 10591.8) * mm, "end": v(-4165.6, 10363.2) * mm});
            skLineSegment(sketch, "E164.bottom", {"start": v(-6629.4, 9169.4) * mm, "end": v(-6400.8, 9169.4) * mm});
            skLineSegment(sketch, "E164.top", {"start": v(-6629.4, 8280.4) * mm, "end": v(-6400.8, 8280.4) * mm});
            skLineSegment(sketch, "E164.left", {"start": v(-6629.4, 9169.4) * mm, "end": v(-6629.4, 8280.4) * mm});
            skLineSegment(sketch, "E164.right", {"start": v(-6400.8, 9169.4) * mm, "end": v(-6400.8, 8280.4) * mm});
            skLineSegment(sketch, "E165.bottom", {"start": v(-6629.4, 5867.4) * mm, "end": v(-6400.8, 5867.4) * mm});
            skLineSegment(sketch, "E165.top", {"start": v(-6629.4, 4953) * mm, "end": v(-6400.8, 4953) * mm});
            skLineSegment(sketch, "E165.left", {"start": v(-6629.4, 5867.4) * mm, "end": v(-6629.4, 4953) * mm});
            skLineSegment(sketch, "E165.right", {"start": v(-6400.8, 5867.4) * mm, "end": v(-6400.8, 4953) * mm});
            skLineSegment(sketch, "E166.bottom", {"start": v(-6629.4, 3378.2) * mm, "end": v(-6400.8, 3378.2) * mm});
            skLineSegment(sketch, "E166.top", {"start": v(-6629.4, 2489.2) * mm, "end": v(-6400.8, 2489.2) * mm});
            skLineSegment(sketch, "E166.left", {"start": v(-6629.4, 3378.2) * mm, "end": v(-6629.4, 2489.2) * mm});
            skLineSegment(sketch, "E166.right", {"start": v(-6400.8, 3378.2) * mm, "end": v(-6400.8, 2489.2) * mm});
            skLineSegment(sketch, "E167.bottom", {"start": v(-5181.6, 1219.2) * mm, "end": v(-3886.2, 1219.2) * mm});
            skLineSegment(sketch, "E167.top", {"start": v(-5181.6, 990.6) * mm, "end": v(-3886.2, 990.6) * mm});
            skLineSegment(sketch, "E167.left", {"start": v(-5181.6, 1219.2) * mm, "end": v(-5181.6, 990.6) * mm});
            skLineSegment(sketch, "E167.right", {"start": v(-3886.2, 1219.2) * mm, "end": v(-3886.2, 990.6) * mm});
            skLineSegment(sketch, "E168.bottom", {"start": v(1066.8, 0) * mm, "end": v(2794, 0) * mm});
            skLineSegment(sketch, "E168.top", {"start": v(1066.8, -228.6) * mm, "end": v(2794, -228.6) * mm});
            skLineSegment(sketch, "E168.left", {"start": v(1066.8, 0) * mm, "end": v(1066.8, -228.6) * mm});
            skLineSegment(sketch, "E168.right", {"start": v(2794, 0) * mm, "end": v(2794, -228.6) * mm});
            skLineSegment(sketch, "E169.bottom", {"start": v(3810, 5410.2) * mm, "end": v(4038.6, 5410.2) * mm});
            skLineSegment(sketch, "E169.top", {"start": v(3810, 4495.8) * mm, "end": v(4038.6, 4495.8) * mm});
            skLineSegment(sketch, "E169.left", {"start": v(3810, 5410.2) * mm, "end": v(3810, 4495.8) * mm});
            skLineSegment(sketch, "E169.right", {"start": v(4038.6, 5410.2) * mm, "end": v(4038.6, 4495.8) * mm});
            skLineSegment(sketch, "E170.bottom", {"start": v(4038.6, 6705.6) * mm, "end": v(3810, 6705.6) * mm});
            skLineSegment(sketch, "E170.top", {"start": v(4038.6, 7620) * mm, "end": v(3810, 7620) * mm});
            skLineSegment(sketch, "E170.left", {"start": v(4038.6, 6705.6) * mm, "end": v(4038.6, 7620) * mm});
            skLineSegment(sketch, "E170.right", {"start": v(3810, 6705.6) * mm, "end": v(3810, 7620) * mm});
            skLineSegment(sketch, "E171.bottom", {"start": v(1371.6, 10591.8) * mm, "end": v(3098.8, 10591.8) * mm});
            skLineSegment(sketch, "E171.top", {"start": v(1371.6, 10363.2) * mm, "end": v(3098.8, 10363.2) * mm});
            skLineSegment(sketch, "E171.left", {"start": v(1371.6, 10591.8) * mm, "end": v(1371.6, 10363.2) * mm});
            skLineSegment(sketch, "E171.right", {"start": v(3098.8, 10591.8) * mm, "end": v(3098.8, 10363.2) * mm});
            skLineSegment(sketch, "E172.bottom", {"start": v(-2184.4, 10591.8) * mm, "end": v(-863.6, 10591.8) * mm});
            skLineSegment(sketch, "E172.top", {"start": v(-2184.4, 10363.2) * mm, "end": v(-863.6, 10363.2) * mm});
            skLineSegment(sketch, "E172.left", {"start": v(-2184.4, 10591.8) * mm, "end": v(-2184.4, 10363.2) * mm});
            skLineSegment(sketch, "E172.right", {"start": v(-863.6, 10591.8) * mm, "end": v(-863.6, 10363.2) * mm});
            skLineSegment(sketch, "E173.bottom", {"start": v(-685.8, 12750.8) * mm, "end": v(-482.6, 12750.8) * mm});
            skLineSegment(sketch, "E173.top", {"start": v(-685.8, 10642.6) * mm, "end": v(-482.6, 10642.6) * mm});
            skLineSegment(sketch, "E173.left", {"start": v(-685.8, 12750.8) * mm, "end": v(-685.8, 10642.6) * mm});
            skLineSegment(sketch, "E173.right", {"start": v(-482.6, 12750.8) * mm, "end": v(-482.6, 10642.6) * mm});
            skLineSegment(sketch, "E174.bottom", {"start": v(-254, 13182.6) * mm, "end": v(3606.8, 13182.6) * mm});
            skLineSegment(sketch, "E174.top", {"start": v(-254, 12979.4) * mm, "end": v(3606.8, 12979.4) * mm});
            skLineSegment(sketch, "E174.left", {"start": v(-254, 13182.6) * mm, "end": v(-254, 12979.4) * mm});
            skLineSegment(sketch, "E174.right", {"start": v(3606.8, 13182.6) * mm, "end": v(3606.8, 12979.4) * mm});
            skLineSegment(sketch, "E175.bottom", {"start": v(4038.6, 12750.8) * mm, "end": v(3835.4, 12750.8) * mm});
            skLineSegment(sketch, "E175.top", {"start": v(4038.6, 11785.6) * mm, "end": v(3835.4, 11785.6) * mm});
            skLineSegment(sketch, "E175.left", {"start": v(4038.6, 12750.8) * mm, "end": v(4038.6, 11785.6) * mm});
            skLineSegment(sketch, "E175.right", {"start": v(3835.4, 12750.8) * mm, "end": v(3835.4, 11785.6) * mm});
            skLineSegment(sketch, "E176.bottom", {"start": v(4038.6, 10591.8) * mm, "end": v(3835.4, 10591.8) * mm});
            skLineSegment(sketch, "E176.top", {"start": v(4038.6, 10718.8) * mm, "end": v(3835.4, 10718.8) * mm});
            skLineSegment(sketch, "E176.left", {"start": v(4038.6, 10591.8) * mm, "end": v(4038.6, 10718.8) * mm});
            skLineSegment(sketch, "E176.right", {"start": v(3835.4, 10591.8) * mm, "end": v(3835.4, 10718.8) * mm});
            skLineSegment(sketch, "E177.bottom", {"start": v(3606.8, 4114.8) * mm, "end": v(3810, 4114.8) * mm});
            skLineSegment(sketch, "E177.top", {"start": v(3606.8, 2286) * mm, "end": v(3810, 2286) * mm});
            skLineSegment(sketch, "E177.left", {"start": v(3606.8, 4114.8) * mm, "end": v(3606.8, 2286) * mm});
            skLineSegment(sketch, "E177.right", {"start": v(3810, 4114.8) * mm, "end": v(3810, 2286) * mm});
            skLineSegment(sketch, "E178.bottom", {"start": v(-4876.8, 6096) * mm, "end": v(-6400.8, 6096) * mm});
            skLineSegment(sketch, "E178.top", {"start": v(-4876.8, 5994.4) * mm, "end": v(-6400.8, 5994.4) * mm});
            skLineSegment(sketch, "E178.left", {"start": v(-4876.8, 6096) * mm, "end": v(-4876.8, 5994.4) * mm});
            skLineSegment(sketch, "E178.right", {"start": v(-6400.8, 6096) * mm, "end": v(-6400.8, 5994.4) * mm});
            skLineSegment(sketch, "E179", {"start": v(3835.4, 12750.8) * mm, "end": v(3835.4, 12979.4) * mm, "construction": true});
            skLineSegment(sketch, "E180", {"start": v(3835.4, 12979.4) * mm, "end": v(3606.8, 12979.4) * mm, "construction": true});
            skLineSegment(sketch, "E181", {"start": v(-482.6, 12750.8) * mm, "end": v(-482.6, 12979.4) * mm, "construction": true});
            skLineSegment(sketch, "E182", {"start": v(-482.6, 12979.4) * mm, "end": v(-254, 12979.4) * mm, "construction": true});
            skLineSegment(sketch, "E183.bottom", {"start": v(-1066.8, 5029.2) * mm, "end": v(-152.4, 5029.2) * mm});
            skLineSegment(sketch, "E183.top", {"start": v(-1066.8, 3352.8) * mm, "end": v(-152.4, 3352.8) * mm});
            skLineSegment(sketch, "E183.left", {"start": v(-1066.8, 5029.2) * mm, "end": v(-1066.8, 3352.8) * mm});
            skLineSegment(sketch, "E183.right", {"start": v(-152.4, 5029.2) * mm, "end": v(-152.4, 3352.8) * mm});
            skSolve(sketch);
        }
        {
            var Q0;
            Q0=makeQuery(id+"F3.imprint","IMPRINT",FACE,{"disambiguationData":[TD([[makeQuery(id+"F3.imprint","IMPRINT",EDGE,{"derivedFrom":sQuery(id+"F3.wireOp",EDGE,"E173.bottom")}),-1.0]])]});
            var Q1;
            Q1=makeQuery(id+"F3.imprint","IMPRINT",FACE,{"disambiguationData":[TD([[makeQuery(id+"F3.imprint","IMPRINT",EDGE,{"derivedFrom":sQuery(id+"F3.wireOp",EDGE,"E174.bottom")}),-1.0]])]});
            var Q2;
            Q2=makeQuery(id+"F3.imprint","IMPRINT",FACE,{"disambiguationData":[TD([[makeQuery(id+"F3.imprint","IMPRINT",EDGE,{"derivedFrom":sQuery(id+"F3.wireOp",EDGE,"E175.bottom")}),1.0]])]});
            var Q3;
            Q3=makeQuery(id+"F3.imprint","IMPRINT",FACE,{"disambiguationData":[TD([[makeQuery(id+"F3.imprint","IMPRINT",EDGE,{"derivedFrom":sQuery(id+"F3.wireOp",EDGE,"E176.bottom")}),-1.0]])]});
            extrude(context, id + "F4", {"entities" : qUnion([Q0, Q1, Q2, Q3]), "operationType" : NewBodyOperationType.REMOVE, "depth" : 2146.3 * mm, "offsetDistance" : 25.4 * mm, "hasSecondDirection" : true, "secondDirectionOppositeDirection" : false, "secondDirectionDepth" : 647.7 * mm});
        }
        {
            var Q0;
            Q0=makeQuery(id+"F3.imprint","IMPRINT",FACE,{"disambiguationData":[TD([[makeQuery(id+"F3.imprint","IMPRINT",EDGE,{"derivedFrom":sQuery(id+"F3.wireOp",EDGE,"E168.bottom")}),-1.0]])]});
            var Q1;
            Q1=makeQuery(id+"F3.imprint","IMPRINT",FACE,{"disambiguationData":[TD([[makeQuery(id+"F3.imprint","IMPRINT",EDGE,{"derivedFrom":sQuery(id+"F3.wireOp",EDGE,"E171.bottom")}),-1.0]])]});
            var Q2;
            Q2=makeQuery(id+"F3.imprint","IMPRINT",FACE,{"disambiguationData":[TD([[makeQuery(id+"F3.imprint","IMPRINT",EDGE,{"derivedFrom":sQuery(id+"F3.wireOp",EDGE,"E167.bottom")}),-1.0]])]});
            var Q3;
            Q3=makeQuery(id+"F3.imprint","IMPRINT",FACE,{"disambiguationData":[TD([[makeQuery(id+"F3.imprint","IMPRINT",EDGE,{"derivedFrom":sQuery(id+"F3.wireOp",EDGE,"E166.bottom")}),-1.0]])]});
            var Q4;
            Q4=makeQuery(id+"F3.imprint","IMPRINT",FACE,{"disambiguationData":[TD([[makeQuery(id+"F3.imprint","IMPRINT",EDGE,{"derivedFrom":sQuery(id+"F3.wireOp",EDGE,"E164.bottom")}),-1.0]])]});
            var Q5;
            Q5=makeQuery(id+"F3.imprint","IMPRINT",FACE,{"disambiguationData":[TD([[makeQuery(id+"F3.imprint","IMPRINT",EDGE,{"derivedFrom":sQuery(id+"F3.wireOp",EDGE,"E163.bottom")}),-1.0]])]});
            extrude(context, id + "F5", {"entities" : qUnion([Q0, Q1, Q2, Q3, Q4, Q5]), "operationType" : NewBodyOperationType.REMOVE, "depth" : 2082.8 * mm, "offsetDistance" : 25.4 * mm, "hasSecondDirection" : true, "secondDirectionOppositeDirection" : false, "secondDirectionDepth" : 838.2 * mm});
        }
        {
            var Q0;
            Q0=makeQuery(id+"F3.imprint","IMPRINT",FACE,{"disambiguationData":[TD([[makeQuery(id+"F3.imprint","IMPRINT",EDGE,{"derivedFrom":sQuery(id+"F3.wireOp",EDGE,"E165.bottom")}),-1.0]])]});
            var Q1;
            Q1=makeQuery(id+"F3.imprint","IMPRINT",FACE,{"disambiguationData":[TD([[makeQuery(id+"F3.imprint","IMPRINT",EDGE,{"derivedFrom":sQuery(id+"F3.wireOp",EDGE,"E170.bottom")}),-1.0]])]});
            var Q2;
            Q2=makeQuery(id+"F3.imprint","IMPRINT",FACE,{"disambiguationData":[TD([[makeQuery(id+"F3.imprint","IMPRINT",EDGE,{"derivedFrom":sQuery(id+"F3.wireOp",EDGE,"E169.bottom")}),-1.0]])]});
            var Q3;
            Q3=makeQuery(id+"F3.imprint","IMPRINT",FACE,{"disambiguationData":[TD([[makeQuery(id+"F3.imprint","IMPRINT",EDGE,{"derivedFrom":sQuery(id+"F3.wireOp",EDGE,"E172.bottom")}),-1.0]])]});
            extrude(context, id + "F6", {"entities" : qUnion([Q0, Q1, Q2, Q3]), "operationType" : NewBodyOperationType.REMOVE, "depth" : 2082.8 * mm, "offsetDistance" : 25.4 * mm, "hasSecondDirection" : true, "secondDirectionOppositeDirection" : false, "secondDirectionDepth" : 1143 * mm});
        }
        {
            var Q0;
            Q0=makeQuery(id+"F3.imprint","IMPRINT",FACE,{"disambiguationData":[TD([[makeQuery(id+"F3.imprint","IMPRINT",EDGE,{"derivedFrom":sQuery(id+"F3.wireOp",EDGE,"E183.bottom")}),-1.0]])]});
            extrude(context, id + "F7", {"entities" : qUnion([Q0]), "operationType" : NewBodyOperationType.REMOVE, "oppositeDirection" : true, "depth" : 50.8 * mm, "offsetDistance" : 25.4 * mm});
        }
        {
            var Q0;
            Q0=makeQuery(id+"F3.imprint","IMPRINT",FACE,{"disambiguationData":[TD([[makeQuery(id+"F3.imprint","IMPRINT",EDGE,{"derivedFrom":sQuery(id+"F3.wireOp",EDGE,"E177.bottom")}),-1.0]])]});
            extrude(context, id + "F8", {"entities" : qUnion([Q0]), "operationType" : NewBodyOperationType.ADD, "depth" : 1320.8 * mm, "offsetDistance" : 25.4 * mm, "hasSecondDirection" : true, "secondDirectionOppositeDirection" : false, "secondDirectionDepth" : 1168.4 * mm});
        }
        {
            var Q0;
            Q0=makeQuery(id+"F0.imprint","IMPRINT",FACE,{"disambiguationData":[TD([[makeQuery(id+"F0.imprint","IMPRINT",EDGE,{"derivedFrom":sQuery(id+"F0.wireOp",EDGE,"E38")}),1.0]])]});
            extrude(context, id + "F9", {"entities" : qUnion([Q0]), "operationType" : NewBodyOperationType.REMOVE, "depth" : 1879.6 * mm, "offsetDistance" : 25.4 * mm, "hasSecondDirection" : true, "secondDirectionOppositeDirection" : false, "secondDirectionDepth" : 1270 * mm});
        }
        {
            var Q0;
            {var subQ2=sQuery(id+"F3.wireOp",EDGE,"E150");Q0=makeQuery(id+"F3.imprint","IMPRINT",FACE,{"disambiguationData":[TD([[makeQuery(id+"F3.imprint","IMPRINT",EDGE,{"derivedFrom":subQ2}),-1.0]])]});}
            var Q1;
            {var subQ0=sQuery(id+"F3.wireOp",EDGE,"E162.top");Q1=makeQuery(id+"F3.imprint","IMPRINT",FACE,{"disambiguationData":[TD([[makeQuery(id+"F3.imprint","IMPRINT",EDGE,{"derivedFrom":subQ0}),1.0]])]});}
            extrude(context, id + "F10", {"entities" : qUnion([Q0, Q1]), "operationType" : NewBodyOperationType.ADD, "depth" : 863.6 * mm, "offsetDistance" : 25.4 * mm});
        }
        {
            var Q0;
            {var subQ0=sQuery(id+"F3.wireOp",EDGE,"E162.top");Q0=makeQuery(id+"F3.imprint","IMPRINT",FACE,{"disambiguationData":[TD([[makeQuery(id+"F3.imprint","IMPRINT",EDGE,{"derivedFrom":subQ0}),1.0]])]});}
            extrude(context, id + "F11", {"entities" : qUnion([Q0]), "operationType" : NewBodyOperationType.ADD, "depth" : 2108.2 * mm, "offsetDistance" : 25.4 * mm, "hasSecondDirection" : true, "secondDirectionOppositeDirection" : false, "secondDirectionDepth" : 1346.2 * mm});
        }
        {
            var Q0;
            Q0=makeQuery(id+"F3.imprint","IMPRINT",FACE,{"disambiguationData":[TD([[makeQuery(id+"F3.imprint","IMPRINT",EDGE,{"derivedFrom":sQuery(id+"F3.wireOp",EDGE,"E178.bottom")}),1.0]])]});
            extrude(context, id + "F12", {"entities" : qUnion([Q0]), "operationType" : NewBodyOperationType.ADD, "depth" : 381 * mm, "offsetDistance" : 25.4 * mm});
        }
        {
            var Q0;
            Q0=makeQuery(id+"F1.opExtrude","SWEPT_BODY",BODY,{"disambiguationData":[OSD([sQuery(id+"F0.wireOp",EDGE,"E0.bottom"),sQuery(id+"F0.wireOp",EDGE,"E0.left"),sQuery(id+"F0.wireOp",EDGE,"E0.right"),sQuery(id+"F0.wireOp",EDGE,"E1.bottom"),sQuery(id+"F0.wireOp",EDGE,"E2.1"),sQuery(id+"F0.wireOp",EDGE,"E2.2"),sQuery(id+"F0.wireOp",EDGE,"E2.4"),sQuery(id+"F0.wireOp",EDGE,"E2.5"),sQuery(id+"F0.wireOp",EDGE,"E33"),sQuery(id+"F0.wireOp",EDGE,"E57"),sQuery(id+"F0.wireOp",EDGE,"E58"),sQuery(id+"F0.wireOp",EDGE,"E59"),sQuery(id+"F0.wireOp",EDGE,"E76"),sQuery(id+"F0.wireOp",EDGE,"E77"),sQuery(id+"F0.wireOp",EDGE,"E78"),sQuery(id+"F0.wireOp",EDGE,"E112"),sQuery(id+"F0.wireOp",EDGE,"E114.trimOffspring"),sQuery(id+"F0.wireOp",EDGE,"E115.trimOffspring"),sQuery(id+"F0.wireOp",EDGE,"E119"),sQuery(id+"F0.wireOp",EDGE,"E120"),sQuery(id+"F0.wireOp",EDGE,"E121"),sQuery(id+"F0.wireOp",EDGE,"E122"),sQuery(id+"F0.wireOp",EDGE,"E123"),sQuery(id+"F0.wireOp",EDGE,"E124"),sQuery(id+"F0.wireOp",EDGE,"E128.trimOffspring"),sQuery(id+"F0.wireOp",EDGE,"E131"),sQuery(id+"F0.wireOp",EDGE,"E134"),sQuery(id+"F0.wireOp",EDGE,"E138"),sQuery(id+"F0.wireOp",EDGE,"E144"),sQuery(id+"F0.wireOp",EDGE,"E145"),sQuery(id+"F0.wireOp",EDGE,"E148")])]});
            var Q1;
            Q1=qCreatedBy(makeId("Origin.pointOp"),VERTEX);
            transform(context, id + "F13", {"entities" : qUnion([Q0]), "transformType" : TransformType.SCALE_UNIFORMLY, "scale" : 1 / 40, "scalePoint" : qUnion([Q1]), "makeCopy" : false});
        }
    });
